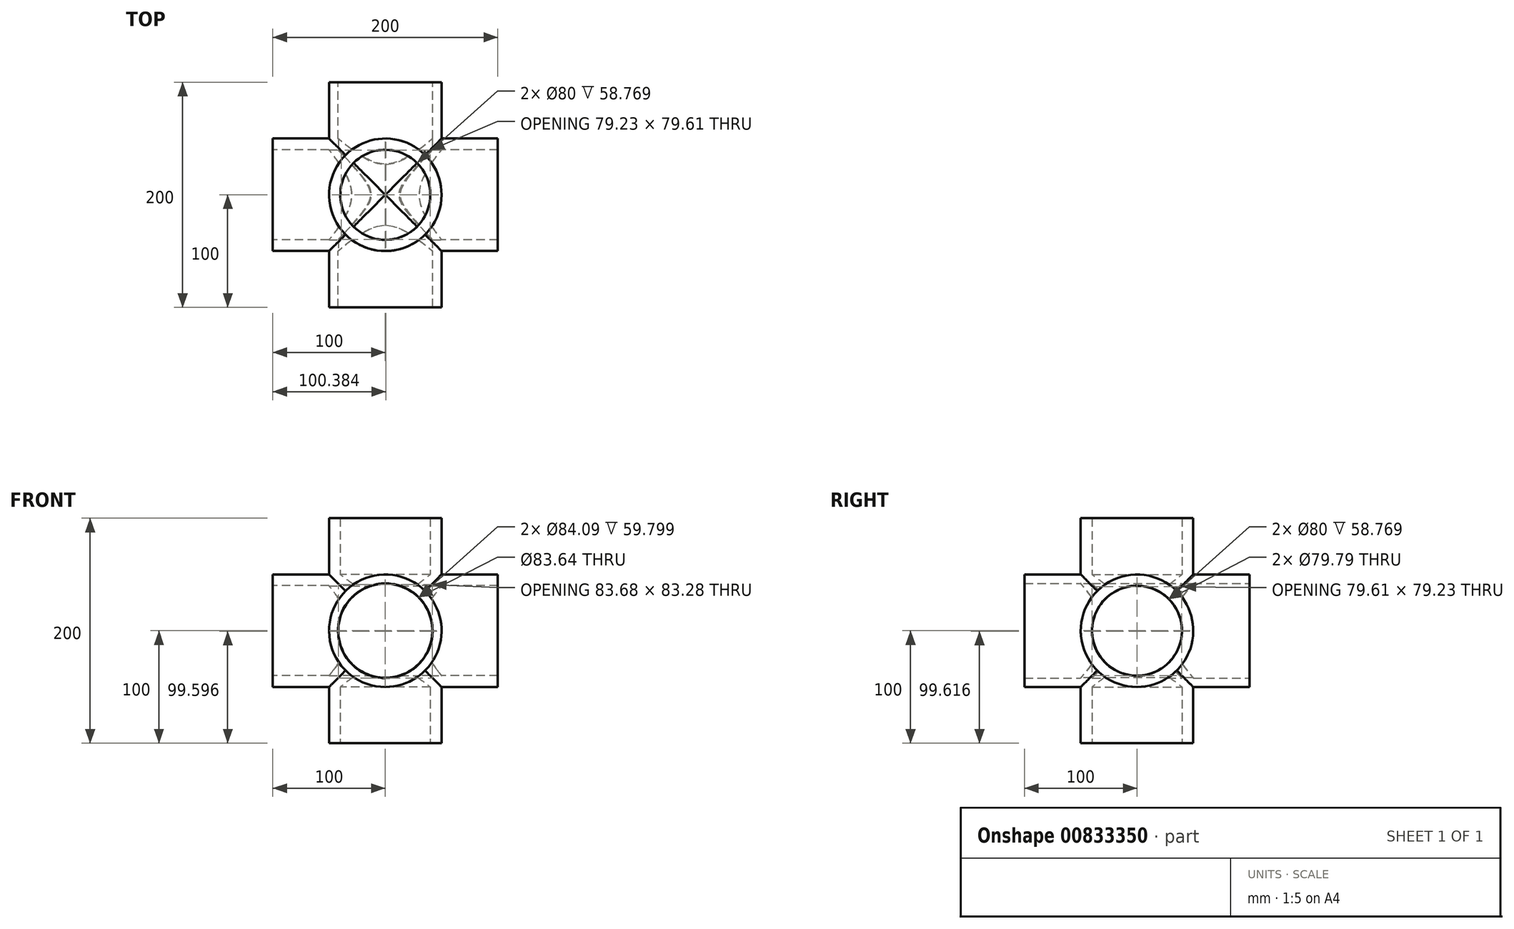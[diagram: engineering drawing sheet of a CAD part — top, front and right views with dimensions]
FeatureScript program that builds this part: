
annotation { "Feature Type Name" : "Feature", "Feature Type Description" : "" }
export const myFeature = defineFeature(function(context is Context, id is Id, definition is map)
    precondition{}
    {
        {
            var Q0;
            Q0=qCreatedBy(makeId("Front.planeOp"),FACE);
            var sketch = newSketch(context, id + "F0", { "sketchPlane" : qUnion([Q0])});
            skCircle(sketch, "E0", {"center": v(0, 0) * mm, "radius": 50 * mm});
            skCircle(sketch, "E1", {"center": v(0, 0) * mm, "radius": 42.04 * mm});
            skSolve(sketch);
        }
        {
            var Q0;
            Q0=qCreatedBy(makeId("Top.planeOp"),FACE);
            var sketch = newSketch(context, id + "F1", { "sketchPlane" : qUnion([Q0])});
            skCircle(sketch, "E2", {"center": v(0, 0) * mm, "radius": 50 * mm});
            skCircle(sketch, "E3", {"center": v(0, 0) * mm, "radius": 40 * mm});
            skSolve(sketch);
        }
        {
            var Q0;
            Q0=qCreatedBy(makeId("Right.planeOp"),FACE);
            var sketch = newSketch(context, id + "F2", { "sketchPlane" : qUnion([Q0])});
            skCircle(sketch, "E4", {"center": v(0, 0) * mm, "radius": 50 * mm});
            skCircle(sketch, "E5", {"center": v(0, 0) * mm, "radius": 40 * mm});
            skSolve(sketch);
        }
        {
            var Q0;
            Q0=makeQuery(id+"F2.imprint","IMPRINT",FACE,{"disambiguationData":[TD([[makeQuery(id+"F2.imprint","IMPRINT",EDGE,{"derivedFrom":sQuery(id+"F2.wireOp",EDGE,"E4")}),1.0]])]});
            extrude(context, id + "F3", {"entities" : qUnion([Q0]), "depth" : 100 * mm, "offsetDistance" : 25 * mm, "hasSecondDirection" : true, "secondDirectionOppositeDirection" : true, "secondDirectionDepth" : 100 * mm});
        }
        {
            var Q0;
            Q0 = qSketchRegion(id + "F0", true);
            extrude(context, id + "F4", {"entities" : qUnion([Q0]), "operationType" : NewBodyOperationType.ADD, "depth" : 100 * mm, "offsetDistance" : 25 * mm, "hasSecondDirection" : true, "secondDirectionOppositeDirection" : true, "secondDirectionDepth" : 100 * mm});
        }
        {
            var Q0;
            Q0 = qSketchRegion(id + "F1", true);
            extrude(context, id + "F5", {"entities" : qUnion([Q0]), "operationType" : NewBodyOperationType.ADD, "depth" : 100 * mm, "offsetDistance" : 25 * mm, "hasSecondDirection" : true, "secondDirectionOppositeDirection" : true, "secondDirectionDepth" : 100 * mm});
        }
        {
            var Q0;
            Q0=makeQuery(id+"F4.opExtrude","CAP_FACE",FACE,{"disambiguationData":[OSD([sQuery(id+"F0.wireOp",EDGE,"E0"),sQuery(id+"F0.wireOp",EDGE,"E1")])],"isStart":false});
            var sketch = newSketch(context, id + "F6", { "sketchPlane" : qUnion([Q0])});
            skCircle(sketch, "E6", {"center": v(0, 0) * mm, "radius": 41.82 * mm});
            skSolve(sketch);
        }
        {
            var Q0;
            Q0=makeQuery(id+"F6.imprint","IMPRINT",FACE,{"disambiguationData":[TD([[makeQuery(id+"F6.imprint","IMPRINT",EDGE,{"derivedFrom":sQuery(id+"F6.wireOp",EDGE,"E6")}),1.0]])]});
            var Q1;
            Q1=sQuery(id+"F6.wireOp",EDGE,"E6");
            extrude(context, id + "F7", {"entities" : qUnion([Q0]), "operationType" : NewBodyOperationType.REMOVE, "surfaceEntities" : qUnion([Q1]), "endBound" : BoundingType.THROUGH_ALL, "oppositeDirection" : true, "depth" : 25 * mm, "offsetDistance" : 25 * mm});
        }
        {
            var Q0;
            Q0=makeQuery(id+"F3.opExtrude","CAP_FACE",FACE,{"disambiguationData":[OSD([sQuery(id+"F2.wireOp",EDGE,"E4"),sQuery(id+"F2.wireOp",EDGE,"E5")])],"isStart":false});
            var sketch = newSketch(context, id + "F8", { "sketchPlane" : qUnion([Q0])});
            skCircle(sketch, "E7", {"center": v(0, 0) * mm, "radius": 39.9 * mm});
            skSolve(sketch);
        }
        {
            var Q0;
            Q0=makeQuery(id+"F8.imprint","IMPRINT",FACE,{"disambiguationData":[TD([[makeQuery(id+"F8.imprint","IMPRINT",EDGE,{"derivedFrom":sQuery(id+"F8.wireOp",EDGE,"E7")}),1.0]])]});
            extrude(context, id + "F9", {"entities" : qUnion([Q0]), "operationType" : NewBodyOperationType.REMOVE, "endBound" : BoundingType.THROUGH_ALL, "oppositeDirection" : true, "depth" : 25 * mm, "offsetDistance" : 25 * mm});
        }
    });
